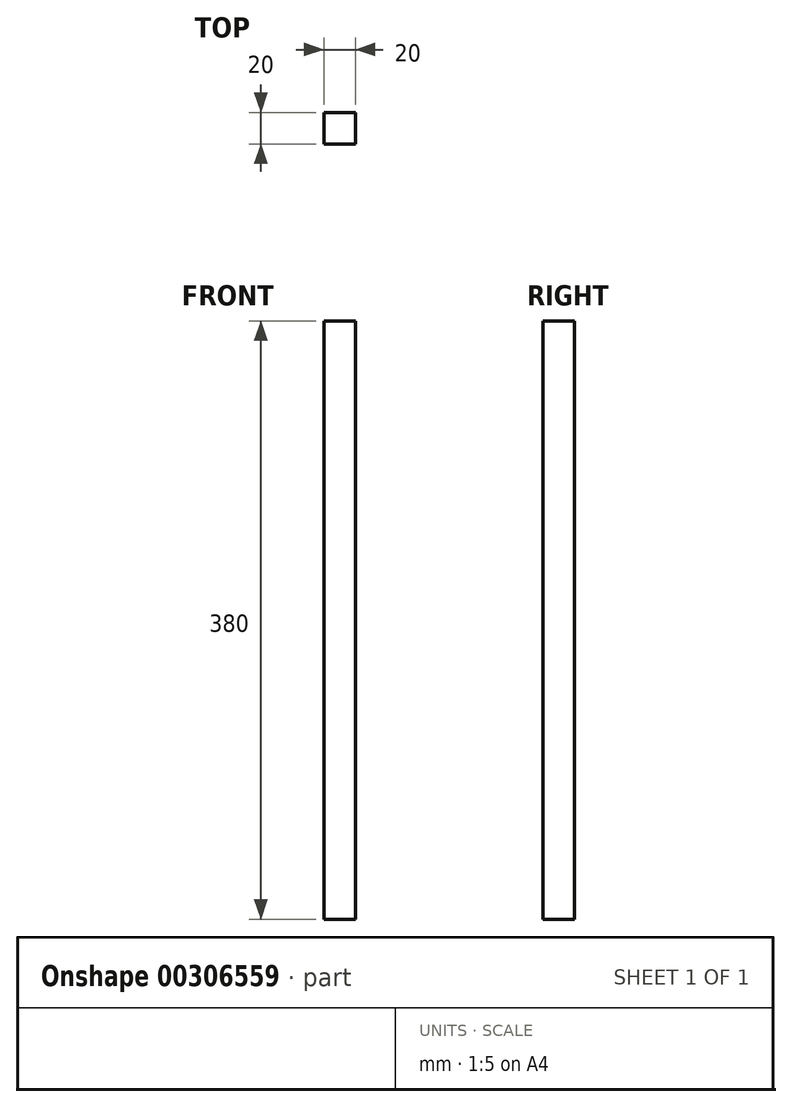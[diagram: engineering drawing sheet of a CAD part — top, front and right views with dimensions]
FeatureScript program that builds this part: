
annotation { "Feature Type Name" : "Feature", "Feature Type Description" : "" }
export const myFeature = defineFeature(function(context is Context, id is Id, definition is map)
    precondition{}
    {
        {
            var Q0;
            Q0=qCreatedBy(makeId("Front.planeOp"),FACE);
            var sketch = newSketch(context, id + "F0", { "sketchPlane" : qUnion([Q0])});
            skLineSegment(sketch, "E0.bottom", {"start": v(0, 0) * mm, "end": v(20, 0) * mm});
            skLineSegment(sketch, "E0.top", {"start": v(0, -380) * mm, "end": v(20, -380) * mm});
            skLineSegment(sketch, "E0.left", {"start": v(0, 0) * mm, "end": v(0, -380) * mm});
            skLineSegment(sketch, "E0.right", {"start": v(20, 0) * mm, "end": v(20, -380) * mm});
            skSolve(sketch);
        }
        {
            var Q0;
            Q0=makeQuery(id+"F0.imprint","IMPRINT",FACE,{"disambiguationData":[TD([[makeQuery(id+"F0.imprint","IMPRINT",EDGE,{"derivedFrom":sQuery(id+"F0.wireOp",EDGE,"E0.bottom")}),-1.0]])]});
            var sketch = newSketch(context, id + "F1", { "sketchPlane" : qUnion([Q0])});
            skSolve(sketch);
        }
        {
            var Q0;
            Q0=makeQuery(id+"F1.imprint","IMPRINT",FACE,{"disambiguationData":[TD([[makeQuery(id+"F1.imprint","IMPRINT",EDGE,{"derivedFrom":makeQuery(id+"F0.imprint","IMPRINT",EDGE,{"derivedFrom":sQuery(id+"F0.wireOp",EDGE,"E0.bottom")})}),-1.0]])]});
            extrude(context, id + "F2", {"entities" : qUnion([Q0]), "depth" : 20 * mm});
        }
    });
